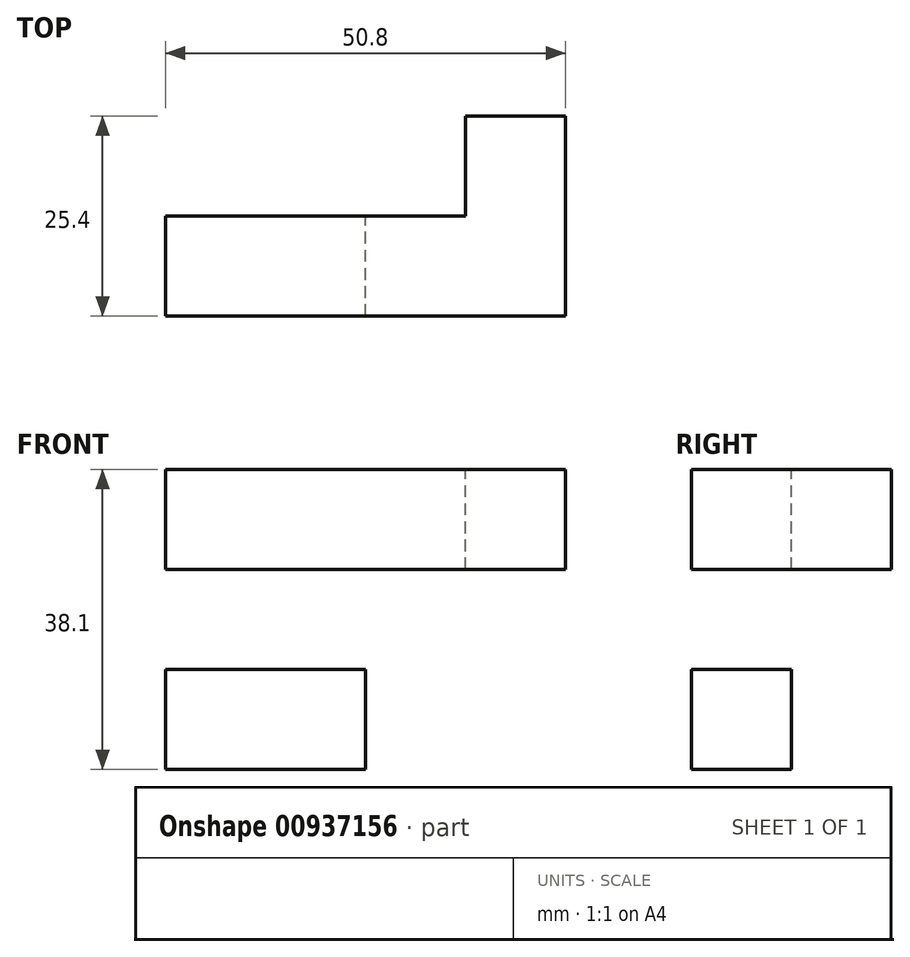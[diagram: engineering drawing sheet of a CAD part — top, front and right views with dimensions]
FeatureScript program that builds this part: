
annotation { "Feature Type Name" : "Feature", "Feature Type Description" : "" }
export const myFeature = defineFeature(function(context is Context, id is Id, definition is map)
    precondition{}
    {
        {
            var Q0;
            Q0=qCreatedBy(makeId("Front.planeOp"),FACE);
            var sketch = newSketch(context, id + "F0", { "sketchPlane" : qUnion([Q0])});
            skLineSegment(sketch, "E0.bottom", {"start": v(-54.9, 29.94) * mm, "end": v(-42.2, 29.94) * mm});
            skLineSegment(sketch, "E0.top", {"start": v(-54.9, 17.24) * mm, "end": v(-42.2, 17.24) * mm});
            skLineSegment(sketch, "E0.left", {"start": v(-54.9, 29.94) * mm, "end": v(-54.9, 17.24) * mm});
            skLineSegment(sketch, "E0.right", {"start": v(-42.2, 29.94) * mm, "end": v(-42.2, 17.24) * mm});
            skLineSegment(sketch, "E1.bottom", {"start": v(-54.9, 17.24) * mm, "end": v(-67.6, 17.24) * mm});
            skLineSegment(sketch, "E1.top", {"start": v(-54.9, 29.94) * mm, "end": v(-67.6, 29.94) * mm});
            skLineSegment(sketch, "E1.left", {"start": v(-54.9, 17.24) * mm, "end": v(-54.9, 29.94) * mm});
            skLineSegment(sketch, "E1.right", {"start": v(-67.6, 17.24) * mm, "end": v(-67.6, 29.94) * mm});
            skLineSegment(sketch, "E2.bottom", {"start": v(-67.6, 29.94) * mm, "end": v(-54.9, 29.94) * mm});
            skLineSegment(sketch, "E2.top", {"start": v(-67.6, 42.64) * mm, "end": v(-54.9, 42.64) * mm});
            skLineSegment(sketch, "E2.left", {"start": v(-67.6, 29.94) * mm, "end": v(-67.6, 42.64) * mm});
            skLineSegment(sketch, "E2.right", {"start": v(-54.9, 29.94) * mm, "end": v(-54.9, 42.64) * mm});
            skLineSegment(sketch, "E3.top", {"start": v(-67.6, 55.34) * mm, "end": v(-54.9, 55.34) * mm});
            skLineSegment(sketch, "E3.left", {"start": v(-67.6, 42.64) * mm, "end": v(-67.6, 55.34) * mm});
            skLineSegment(sketch, "E3.right", {"start": v(-54.9, 42.64) * mm, "end": v(-54.9, 55.34) * mm});
            skLineSegment(sketch, "E4.bottom", {"start": v(-54.9, 42.64) * mm, "end": v(-42.2, 42.64) * mm});
            skLineSegment(sketch, "E4.top", {"start": v(-54.9, 55.34) * mm, "end": v(-42.2, 55.34) * mm});
            skLineSegment(sketch, "E4.right", {"start": v(-42.2, 42.64) * mm, "end": v(-42.2, 55.34) * mm});
            skLineSegment(sketch, "E5.bottom", {"start": v(-42.2, 42.64) * mm, "end": v(-29.5, 42.64) * mm});
            skLineSegment(sketch, "E5.top", {"start": v(-42.2, 55.34) * mm, "end": v(-29.5, 55.34) * mm});
            skLineSegment(sketch, "E5.right", {"start": v(-29.5, 42.64) * mm, "end": v(-29.5, 55.34) * mm});
            skLineSegment(sketch, "E6.bottom", {"start": v(-29.5, 42.64) * mm, "end": v(-16.8, 42.64) * mm});
            skLineSegment(sketch, "E6.top", {"start": v(-29.5, 55.34) * mm, "end": v(-16.8, 55.34) * mm});
            skLineSegment(sketch, "E6.right", {"start": v(-16.8, 42.64) * mm, "end": v(-16.8, 55.34) * mm});
            skSolve(sketch);
        }
        {
            var Q0;
            Q0=makeQuery(id+"F0.imprint","IMPRINT",FACE,{"disambiguationData":[TD([[makeQuery(id+"F0.imprint","IMPRINT",EDGE,{"derivedFrom":sQuery(id+"F0.wireOp",EDGE,"E6.bottom")}),1.0]])]});
            extrude(context, id + "F1", {"entities" : qUnion([Q0]), "endBound" : BoundingType.SYMMETRIC, "depth" : 25.4 * mm, "offsetDistance" : 25.4 * mm});
        }
        {
            var Q0;
            Q0=makeQuery(id+"F0.imprint","IMPRINT",FACE,{"disambiguationData":[TD([[makeQuery(id+"F0.imprint","IMPRINT",EDGE,{"derivedFrom":sQuery(id+"F0.wireOp",EDGE,"E5.bottom")}),1.0]])]});
            var Q1;
            Q1=makeQuery(id+"F0.imprint","IMPRINT",FACE,{"disambiguationData":[TD([[makeQuery(id+"F0.imprint","IMPRINT",EDGE,{"derivedFrom":sQuery(id+"F0.wireOp",EDGE,"E4.bottom")}),1.0]])]});
            var Q2;
            Q2=makeQuery(id+"F0.imprint","IMPRINT",FACE,{"disambiguationData":[TD([[makeQuery(id+"F0.imprint","IMPRINT",EDGE,{"derivedFrom":sQuery(id+"F0.wireOp",EDGE,"E2.top")}),1.0]])]});
            var Q3;
            Q3=makeQuery(id+"F0.imprint","IMPRINT",FACE,{"disambiguationData":[TD([[makeQuery(id+"F0.imprint","IMPRINT",EDGE,{"derivedFrom":sQuery(id+"F0.wireOp",EDGE,"E2.bottom")}),1.0]])]});
            var Q4;
            Q4=makeQuery(id+"F0.imprint","IMPRINT",FACE,{"disambiguationData":[TD([[makeQuery(id+"F0.imprint","IMPRINT",EDGE,{"derivedFrom":sQuery(id+"F0.wireOp",EDGE,"E1.bottom")}),-1.0]])]});
            var Q5;
            Q5=makeQuery(id+"F0.imprint","IMPRINT",FACE,{"disambiguationData":[TD([[makeQuery(id+"F0.imprint","IMPRINT",EDGE,{"derivedFrom":sQuery(id+"F0.wireOp",EDGE,"E0.bottom")}),-1.0]])]});
            extrude(context, id + "F2", {"entities" : qUnion([Q0, Q1, Q2, Q3, Q4, Q5]), "operationType" : NewBodyOperationType.ADD, "depth" : 12.7 * mm, "offsetDistance" : 25.4 * mm});
        }
    });
